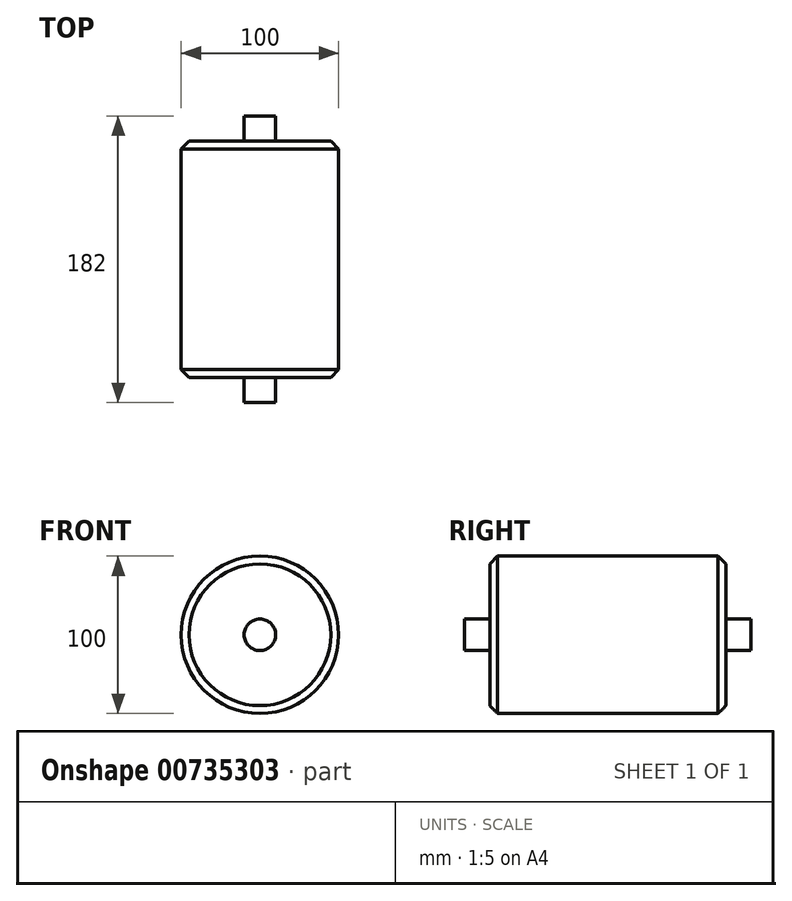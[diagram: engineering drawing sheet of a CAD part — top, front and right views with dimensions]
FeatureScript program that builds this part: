
annotation { "Feature Type Name" : "Feature", "Feature Type Description" : "" }
export const myFeature = defineFeature(function(context is Context, id is Id, definition is map)
    precondition{}
    {
        {
            var Q0;
            Q0=qCreatedBy(makeId("Front.planeOp"),FACE);
            var sketch = newSketch(context, id + "F0", { "sketchPlane" : qUnion([Q0])});
            skCircle(sketch, "E0", {"center": v(0, 0) * mm, "radius": 10 * mm});
            skSolve(sketch);
        }
        {
            var Q0;
            Q0=makeQuery(id+"F0.imprint","IMPRINT",FACE,{"disambiguationData":[TD([[makeQuery(id+"F0.imprint","IMPRINT",EDGE,{"derivedFrom":sQuery(id+"F0.wireOp",EDGE,"E0")}),1.0]])]});
            extrude(context, id + "F1", {"entities" : qUnion([Q0]), "endBound" : BoundingType.SYMMETRIC, "depth" : 182 * mm, "offsetDistance" : 25 * mm});
        }
        {
            var Q0;
            Q0=qCreatedBy(makeId("Front.planeOp"),FACE);
            var sketch = newSketch(context, id + "F2", { "sketchPlane" : qUnion([Q0])});
            skCircle(sketch, "E1", {"center": v(0, 0) * mm, "radius": 50 * mm});
            skSolve(sketch);
        }
        {
            var Q0;
            Q0 = qSketchRegion(id + "F2", true);
            extrude(context, id + "F3", {"entities" : qUnion([Q0]), "operationType" : NewBodyOperationType.ADD, "endBound" : BoundingType.SYMMETRIC, "depth" : 150 * mm, "offsetDistance" : 25 * mm});
        }
        {
            var Q0;
            Q0=makeQuery(id+"F3.opExtrude","CAP_EDGE",EDGE,{"disambiguationData":[OSD([sQuery(id+"F2.wireOp",EDGE,"E1")])],"isStart":true});
            chamfer(context, id + "F4", {"entities" : qUnion([Q0]), "width" : 5 * mm, "tangentPropagation" : true});
        }
        {
            var Q0;
            Q0=makeQuery(id+"F3.opExtrude","CAP_EDGE",EDGE,{"disambiguationData":[OSD([sQuery(id+"F2.wireOp",EDGE,"E1")])],"isStart":false});
            chamfer(context, id + "F5", {"entities" : qUnion([Q0]), "width" : 5 * mm, "tangentPropagation" : true});
        }
    });
